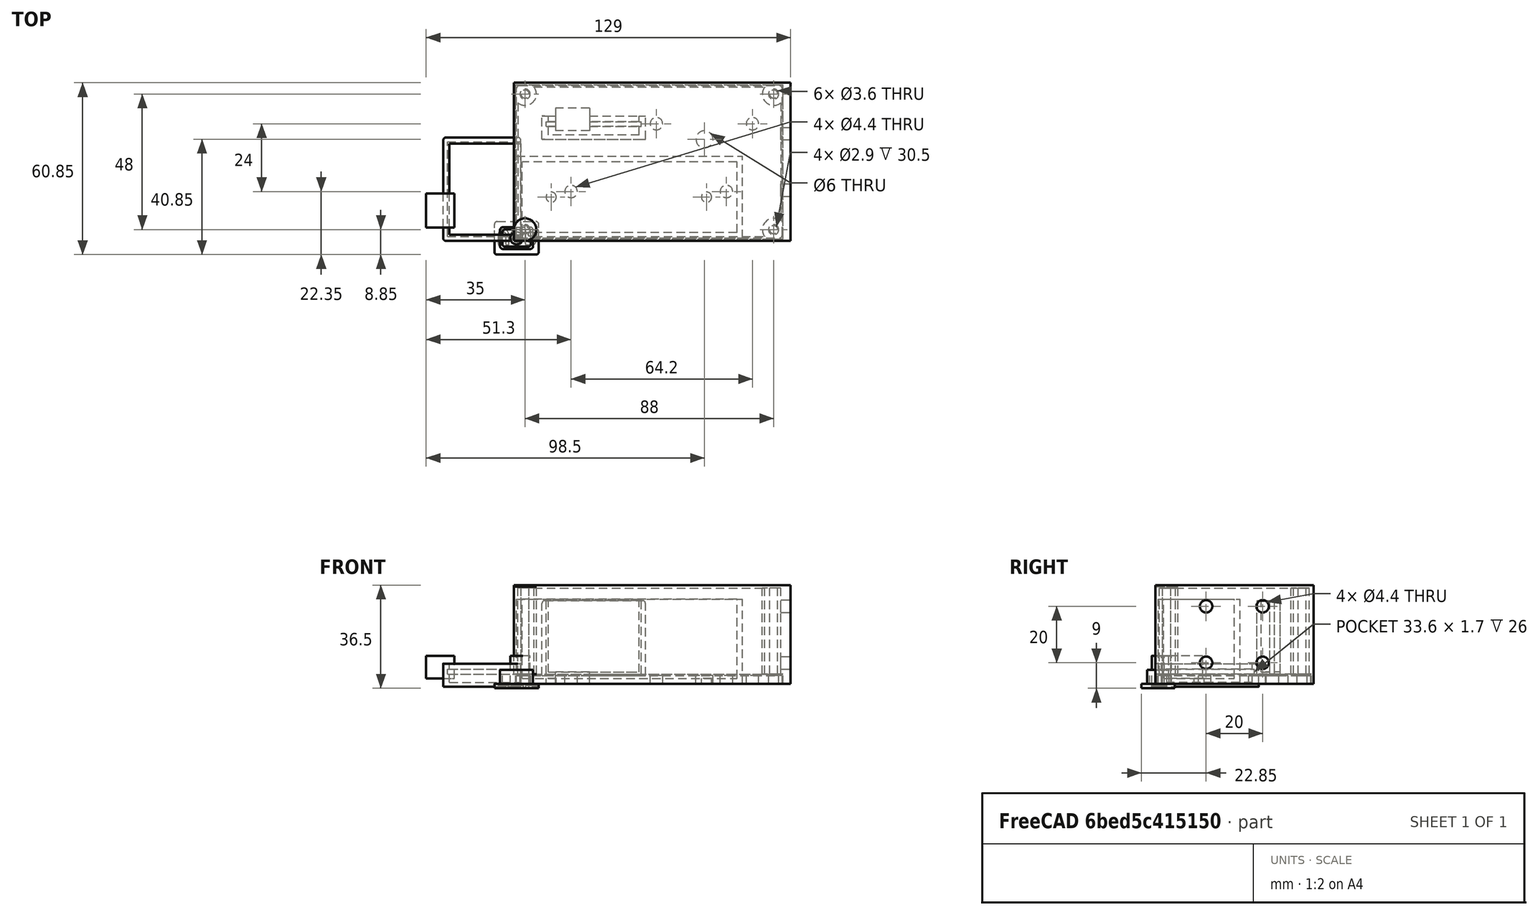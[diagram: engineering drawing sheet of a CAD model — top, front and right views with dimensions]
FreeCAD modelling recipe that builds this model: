
FCSTD DOCUMENT  (FreeCAD 0.19R)
Label: battery_box
License: All rights reserved
LicenseURL: http://en.wikipedia.org/wiki/All_rights_reserved
objects: Part::Box×13, Part::Cylinder×10, Part::MultiFuse×7, Part::Cut×7, App::Part×6, Part::FeaturePython×5, Part::Fillet×5, Part::Feature×1, Spreadsheet::Sheet×1, Part::Part2DObjectPython×1, Part::Extrusion×1
note: 46 computed .brp shape members not serialized (recipe doc carries the construction recipe); baked Part::Feature solids carry a one-line shape summary decoded from their .brp

FEATURE [Part::Box] Box  label="Cube"
  AttacherType = Attacher::AttachEngine3D
  Height = 30
  Length = 80
  Width = 29
FEATURE [Part::Box] Box001  label="Cube001"
  AttacherType = Attacher::AttachEngine3D
  Height = 30
  Length = 76
  Placement = pos=(2,2,2) rot=(0,0,-1;0rad)
  Width = 25
FEATURE [Part::Cylinder] Cylinder
  Angle = 360
  AttacherType = Attacher::AttachEngine3D
  Height = 50
  Placement = pos=(12.25,14.5,-10) rot=(0,0,1;0rad)
  Radius = 1.8
FEATURE [Part::FeaturePython] Array  # Draft array (typed FeaturePython)
  Angle = 360
  ArrayType = 0
  Axis = (0,0,1)
  Base = -> Cylinder
  Center = (0,0,0)
  Fuse = false
  IntervalAxis = (0,0,0)
  IntervalX = (55,0,0)
  IntervalY = (0,1,0)
  IntervalZ = (0,0,1)
  NumberPolar = 1
  NumberX = 2
  NumberY = 1
  NumberZ = 1
FEATURE [Part::MultiFuse] Fusion
  Shapes = -> [Box001,Array]
FEATURE [Part::Cut] Cut
  Base = -> Box
  Tool = -> Fusion
FEATURE [App::Part] Part  label="battery mockup"
  Group = -> [Box001,Box,Cut,Cylinder,Array,Fusion]
  Origin = -> Origin
  Placement = pos=(7,2,2) rot=(0,0,1;0rad)
FEATURE [Part::Feature] usb_female_case_bottom_v2001001001
  Placement = pos=(55,52,3) rot=(1,0,0;3.14159rad)
  shape: bbox 48.8 x 22.97 x 8 mm, 1376 faces, 0 solids (baked)
FEATURE [Part::Box] Box022  label="face plate"
  AttacherType = Attacher::AttachEngine3D
  Height = 3
  Length = 94
  Width = 54
FEATURE [Part::Box] Box024  label="lion micro usb hole"
  AttacherType = Attacher::AttachEngine3D
  Height = 8
  Length = 12
  Placement = pos=(-32,15.8,2) rot=(0,0,-1;1.5708rad)
  Width = 10
FEATURE [App::Part] Part015  label="lion manager mockup hole part"
  Group = -> [Box024]
  Origin = -> Origin022
  Placement = pos=(10,36,27) rot=(0.57735,0.57735,0.57735;4.18879rad)
FEATURE [Part::Cylinder] Cylinder001
  Angle = 360
  AttacherType = Attacher::AttachEngine3D
  Height = 10
  Placement = pos=(19.3,16.5,0) rot=(0,0,1;0rad)
  Radius = 2.2
FEATURE [Part::Cylinder] Cylinder002
  Angle = 360
  AttacherType = Attacher::AttachEngine3D
  Height = 10
  Placement = pos=(74.3,16.5,0) rot=(0,0,1;0rad)
  Radius = 2.2
FEATURE [Part::Box] Box025  label="external cube001"
  AttacherType = Attacher::AttachEngine3D
  Height = 8.2
  Length = 27.5
  Width = 36.6
  expr: Height = <<p>>.bottom_wall + <<p>>.pcb_under + <<p>>.pcb_z + <<p>>.pcb_above
  expr: Width = <<p>>.pcb_y + 2 * <<p>>.side_wall
  expr: Length = <<p>>.pcb_x + <<p>>.side_wall
FEATURE [Part::Fillet] Fillet001  label="external fillet001"
  Base = -> Box025
  Edges = 4 edges r=1: [Edge1,Edge3,Edge5,Edge7]
FEATURE [Part::Box] Box026  label="internal cube001"
  AttacherType = Attacher::AttachEngine3D
  Height = 6.7
  Length = 26.1
  Placement = pos=(2.2,2.2,1.5) rot=(0,0,1;0rad)
  Width = 32.2
  expr: .Placement.Base.y = <<p>>.side_wall + <<p>>.pcb_side_lane
  expr: .Placement.Base.x = <<p>>.side_wall + <<p>>.pcb_side_lane
  expr: .Placement.Base.z = <<p>>.bottom_wall
  expr: Height = <<p>>.pcb_under + <<p>>.pcb_z + <<p>>.pcb_above
  expr: Width = <<p>>.pcb_y - 2 * <<p>>.pcb_side_lane
  expr: Length = <<p>>.pcb_x - 2 * <<p>>.pcb_side_lane + <<p>>.side_wall
FEATURE [Part::Box] Box027  label="pcb extract cube001"
  AttacherType = Attacher::AttachEngine3D
  Height = 1.7
  Length = 26
  Placement = pos=(1.5,1.5,4.5) rot=(0,0,1;0rad)
  Width = 33.6
  expr: .Placement.Base.y = <<p>>.side_wall
  expr: .Placement.Base.x = <<p>>.side_wall
  expr: Length = <<p>>.pcb_x
  expr: Width = <<p>>.pcb_y
  expr: .Placement.Base.z = <<p>>.bottom_wall + <<p>>.pcb_under
  expr: Height = <<p>>.pcb_z
FEATURE [Part::MultiFuse] Fusion003  label="extract fusion001"
  Shapes = -> [Box026,Box027]
FEATURE [Spreadsheet::Sheet] Spreadsheet  label="p"
  cells = A1=pcb_x; B1(pcb_x)=26; A2=pcb_y; B2(pcb_y)=33.6; A3=pcb_z; B3(pcb_z)=1.7; A4=pcb_under; B4(pcb_under)=3; A5=side_wall; B5(side_wall)=1.5; A6=pcb_side_lane; B6(pcb_side_lane)=0.7; A7=bottom_wall; B7(bottom_wall)=1.5; A8=pcb_above; B8(pcb_above)=2
FEATURE [Part::Cut] Cut002  label="lion manager cut"
  Base = -> Fillet001
  Placement = pos=(-26,-1,-1) rot=(0,0,1;0rad)
  Tool = -> Fusion003
FEATURE [App::Part] Part014  label="lion manager mockup part"
  Group = -> [Cut002]
  Origin = -> Origin021
  Placement = pos=(10,36,28) rot=(0.57735,0.57735,0.57735;4.18879rad)
FEATURE [Part::Cylinder] Cylinder003  label="usb attach hole"
  Angle = 360
  AttacherType = Attacher::AttachEngine3D
  Height = 10
  Placement = pos=(83.5,40.5,0) rot=(0,0,1;0rad)
  Radius = 2.2
FEATURE [Part::Cylinder] Cylinder004  label="usb attach hole001"
  Angle = 360
  AttacherType = Attacher::AttachEngine3D
  Height = 10
  Placement = pos=(49.5,40.5,0) rot=(0,0,1;0rad)
  Radius = 2.2
FEATURE [Part::Cylinder] Cylinder005  label="usb attach hole002"
  Angle = 360
  AttacherType = Attacher::AttachEngine3D
  Height = 10
  Placement = pos=(66.5,35,0) rot=(0,0,1;0rad)
  Radius = 3
FEATURE [Part::Cylinder] Cylinder006  label="corner hole"
  Angle = 360
  AttacherType = Attacher::AttachEngine3D
  Height = 10
  Placement = pos=(3,3,0) rot=(0,0,1;0rad)
  Radius = 1.8
FEATURE [Part::FeaturePython] Array001  label="corner hole array"  # Draft array (typed FeaturePython)
  Angle = 360
  ArrayType = 0
  Axis = (0,0,1)
  Base = -> Cylinder006
  Center = (0,0,0)
  Count = 4
  ExpandArray = false
  Fuse = false
  IntervalAxis = (0,0,0)
  IntervalX = (88,0,0)
  IntervalY = (0,48,0)
  IntervalZ = (0,0,100)
  NumberCircles = 3
  NumberPolar = 5
  NumberX = 2
  NumberY = 2
  NumberZ = 1
  PlacementList = 4 placements: [(3,3,0),(3,51,0),(91,3,0),(91,51,0)]
  RadialDistance = 50
  ScaleList = (4) [(1,1,1),(1,1,1),(1,1,1),(1,1,1)]
  Symmetry = 1
  TangentialDistance = 25
FEATURE [Part::MultiFuse] Fusion002  label="hole fusion"
  Shapes = -> [Cylinder001,Cylinder002,Part015,Cylinder003,Cylinder004,Cylinder005,Array001]
FEATURE [Part::Fillet] Fillet  label="bottom plate fillet"
  Base = -> Box022
  Edges = 4 edges r=1: [Edge1,Edge3,Edge5,Edge7]
FEATURE [Part::MultiFuse] Fusion004  label="body fusion"
  Shapes = -> [Part014,Fillet]
FEATURE [Part::Cut] Cut003  label="face body cut"
  Base = -> Fusion004
  Tool = -> Fusion002
FEATURE [Part::Cylinder] Cylinder007  label="stand"
  Angle = 360
  AttacherType = Attacher::AttachEngine3D
  Height = 31
  Placement = pos=(3,3,3.5) rot=(0,0,1;0rad)
  Radius = 4
  expr: Height = <<back external box>>.Height - <<face plate>>.Height - 1mm
  expr: .Placement.Base.z = <<face plate>>.Height + 0.5mm
FEATURE [Part::Box] Box006  label="back internal box"
  AttacherType = Attacher::AttachEngine3D
  Height = 34
  Length = 93
  Placement = pos=(0.5,0.5,0) rot=(0,0,1;0rad)
  Width = 53
  expr: Width = <<face plate>>.Width - 1mm
  expr: Length = <<face plate>>.Length - 1mm
FEATURE [Part::Box] Box005  label="back external box"
  AttacherType = Attacher::AttachEngine3D
  Height = 35
  Length = 98
  Placement = pos=(-1,-1,0) rot=(0,0,1;0rad)
  Width = 56
  expr: Length = <<face plate>>.Length + 4mm
  expr: Width = <<face plate>>.Width + 2mm
  expr: .Placement.Base.x = -(Length - <<face plate>>.Length) / 2 + 1mm
  expr: .Placement.Base.y = -(Width - <<face plate>>.Width) / 2
  expr: Height = <<back internal box>>.Height + 1mm
FEATURE [Part::Cylinder] Cylinder009  label="screw hole002"
  Angle = 360
  AttacherType = Attacher::AttachEngine3D
  Height = 34
  Placement = pos=(3,3,0) rot=(0,0,1;0rad)
  Radius = 1.45
  expr: Height = <<back internal box>>.Height
FEATURE [Part::FeaturePython] Array003  label="screw hole array"  # Draft array (typed FeaturePython)
  Angle = 360
  ArrayType = 0
  Axis = (0,0,1)
  Base = -> Cylinder009
  Center = (0,0,0)
  Count = 4
  ExpandArray = false
  Fuse = false
  IntervalAxis = (0,0,0)
  IntervalX = (88,0,0)
  IntervalY = (0,48,0)
  IntervalZ = (0,0,100)
  NumberCircles = 3
  NumberPolar = 5
  NumberX = 2
  NumberY = 2
  NumberZ = 1
  PlacementList = 4 placements: [(3,3,0),(3,51,0),(91,3,0),(91,51,0)]
  RadialDistance = 50
  ScaleList = (4) [(1,1,1),(1,1,1),(1,1,1),(1,1,1)]
  Symmetry = 1
  TangentialDistance = 25
  expr: .IntervalX.x = <<face plate>>.Length - <<screw hole002>>.Placement.Base.x * 2
  expr: .IntervalY.y = <<face plate>>.Width - <<screw hole002>>.Placement.Base.y * 2
FEATURE [Part::FeaturePython] Array002  label="bolt stand array"  # Draft array (typed FeaturePython)
  Angle = 360
  ArrayType = 0
  Axis = (0,0,1)
  Base = -> Cylinder007
  Center = (0,0,0)
  Count = 4
  ExpandArray = false
  Fuse = false
  IntervalAxis = (0,0,0)
  IntervalX = (88,0,0)
  IntervalY = (0,48,0)
  IntervalZ = (0,0,100)
  NumberCircles = 3
  NumberPolar = 5
  NumberX = 2
  NumberY = 2
  NumberZ = 1
  PlacementList = 4 placements: [(3,3,3.5),(3,51,3.5),(91,3,3.5),(91,51,3.5)]
  RadialDistance = 50
  ScaleList = (4) [(1,1,1),(1,1,1),(1,1,1),(1,1,1)]
  Symmetry = 1
  TangentialDistance = 25
  expr: .IntervalX.x = <<face plate>>.Length - <<screw hole002>>.Placement.Base.x * 2
  expr: .IntervalY.y = <<face plate>>.Width - <<screw hole002>>.Placement.Base.y * 2
FEATURE [Part::Cut] Cut001004  label="bolt stand fusion"
  Base = -> Array002
  Tool = -> Array003
FEATURE [Part::Cylinder] Cylinder010  label="top insert hole"
  Angle = 360
  AttacherType = Attacher::AttachEngine3D
  Height = 10
  Radius = 2.2
FEATURE [Part::FeaturePython] Array004  label="top insert hole array"  # Draft array (typed FeaturePython)
  Angle = 360
  ArrayType = 0
  Axis = (0,0,1)
  Base = -> Cylinder010
  Center = (0,0,0)
  Count = 4
  ExpandArray = false
  Fuse = false
  IntervalAxis = (0,0,0)
  IntervalX = (20,0,0)
  IntervalY = (0,20,0)
  IntervalZ = (0,0,100)
  NumberCircles = 3
  NumberPolar = 5
  NumberX = 2
  NumberY = 2
  NumberZ = 1
  Placement = pos=(91,17,27.5) rot=(0,1,0;1.5708rad)
  PlacementList = 4 placements: [(0,0,0),(0,20,0),(20,0,0),(20,20,0)]
  RadialDistance = 50
  ScaleList = (4) [(1,1,1),(1,1,1),(1,1,1),(1,1,1)]
  Symmetry = 1
  TangentialDistance = 25
FEATURE [Part::Box] Box028  label="outer back internal box"
  AttacherType = Attacher::AttachEngine3D
  Height = 3.5
  Length = 94.6
  Placement = pos=(-0.3,-0.3,0) rot=(0,0,1;0rad)
  Width = 54.6
  expr: Length = <<face plate>>.Length + 0.6mm
  expr: Width = <<face plate>>.Width + 0.6mm
  expr: Height = <<face plate>>.Height + 0.5mm
FEATURE [Part::MultiFuse] Fusion006  label="back box extract fusion"
  Shapes = -> [Box006,Array004,Box028]
FEATURE [Part::Cut] Cut001003  label="back box cut"
  Base = -> Box005
  Tool = -> Fusion006
FEATURE [Part::MultiFuse] Fusion007  label="back box fusion"
  Shapes = -> [Cut001003,Cut001004]
FEATURE [App::Part] Part003004  label="back part"
  Group = -> [Fusion007]
  Origin = -> Origin005
FEATURE [App::Part] Part003005  label="face part"
  Group = -> [Cut003]
  Origin = -> Origin023
FEATURE [Part::Box] Box051015  label="plug cube"
  AttacherType = Attacher::AttachEngine3D
  Height = 5
  Length = 11.7
  Placement = pos=(-5.85,-3.85,0) rot=(0,0,1;0rad)
  Width = 7.7
  expr: .Placement.Base.y = -Width / 2
  expr: .Placement.Base.x = -Length / 2
  expr: Width = <<lion micro usb hole>>.Height - 0.3mm
  expr: Length = <<lion micro usb hole>>.Length - 0.3mm
FEATURE [Part::Box] Box051016  label="plug cube hole"
  AttacherType = Attacher::AttachEngine3D
  Height = 5
  Length = 10.1
  Placement = pos=(-5.05,-3.05,0) rot=(0,0,1;0rad)
  Width = 6.1
  expr: Height = <<plug cube>>.Height
  expr: .Placement.Base.y = -Width / 2
  expr: .Placement.Base.x = -Length / 2
  expr: Width = <<plug cube>>.Width - 1.6mm
  expr: Length = <<plug cube>>.Length - 1.6mm
FEATURE [Part::Fillet] Fillet001012  label="plug cube fillet"
  Base = -> Box051015
  Edges = 4 edges r=1: [Edge1,Edge3,Edge5,Edge7]
FEATURE [Part::Fillet] Fillet001013  label="plug cube hole fillet"
  Base = -> Box051016
  Edges = 4 edges r=1: [Edge1,Edge3,Edge5,Edge7]
FEATURE [Part::Cut] Cut002002007012  label="hole plug cut"
  Base = -> Fillet001012
  Tool = -> Fillet001013
FEATURE [Part::Box] Box051017  label="plug top"
  AttacherType = Attacher::AttachEngine3D
  Height = 1.5
  Length = 15.7
  Placement = pos=(-7.85,-5.85,-1.5) rot=(0,0,1;0rad)
  Width = 11.7
  expr: .Placement.Base.z = -Height
  expr: Length = <<plug cube>>.Length + 4mm
  expr: Width = <<plug cube>>.Width + 4mm
  expr: .Placement.Base.x = -Length / 2
  expr: .Placement.Base.y = -Width / 2
FEATURE [Part::Fillet] Fillet001014  label="plug top fillet"
  Base = -> Box051017
  Edges = 4 edges r=1: [Edge1,Edge3,Edge5,Edge7]
FEATURE [Part::Part2DObjectPython] ShapeString  # Draft 2D object (typed FeaturePython)
  FontFile = <path>
  Placement = pos=(-7,3,-0.5) rot=(1,0,0;3.14159rad)
  Size = 6
  String = USB
  Tracking = 0
FEATURE [Part::Extrusion] Extrude  label="string extrude"
  Base = -> ShapeString
  Dir = (0,-1e-16,-1)
  DirMode = 2
  FaceMakerClass = Part::FaceMakerBullseye
  LengthFwd = 1
  LengthRev = 0
  Solid = false
  Symmetric = false
FEATURE [Part::Cut] Cut002002007013  label="usb plug top cut"
  Base = -> Fillet001014
  Tool = -> Extrude
FEATURE [Part::MultiFuse] Fusion028  label="usb hole plug"
  Shapes = -> [Cut002002007012,Cut002002007013]
FEATURE [App::Part] Part003007  label="usb hole plug part"
  Group = -> [Fusion028]
  Origin = -> Origin024
note: 1 file-system path scrubbed to <path> (originals preserved in the JSON sidecar)
